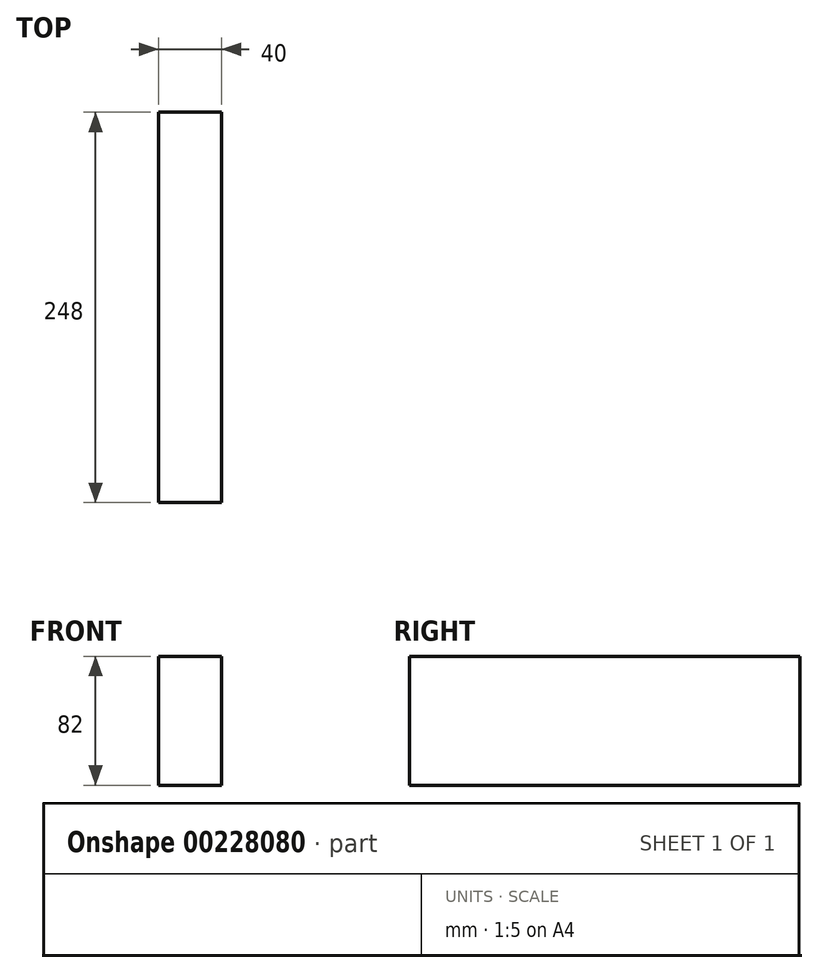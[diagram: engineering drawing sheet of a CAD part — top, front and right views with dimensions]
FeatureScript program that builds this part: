
annotation { "Feature Type Name" : "Feature", "Feature Type Description" : "" }
export const myFeature = defineFeature(function(context is Context, id is Id, definition is map)
    precondition{}
    {
        {
            var Q0;
            Q0=qCreatedBy(makeId("Front.planeOp"),FACE);
            var sketch = newSketch(context, id + "F0", { "sketchPlane" : qUnion([Q0])});
            skLineSegment(sketch, "E0.bottom", {"start": v(0, 0) * mm, "end": v(40, 0) * mm});
            skLineSegment(sketch, "E0.top", {"start": v(0, 82) * mm, "end": v(40, 82) * mm});
            skLineSegment(sketch, "E0.left", {"start": v(0, 0) * mm, "end": v(0, 82) * mm});
            skLineSegment(sketch, "E0.right", {"start": v(40, 0) * mm, "end": v(40, 82) * mm});
            skSolve(sketch);
        }
        {
            var Q0;
            Q0=makeQuery(id+"F0.imprint","IMPRINT",FACE,{"disambiguationData":[TD([[makeQuery(id+"F0.imprint","IMPRINT",EDGE,{"derivedFrom":sQuery(id+"F0.wireOp",EDGE,"E0.bottom")}),1.0]])]});
            extrude(context, id + "F1", {"entities" : qUnion([Q0]), "depth" : 248 * mm});
        }
    });
